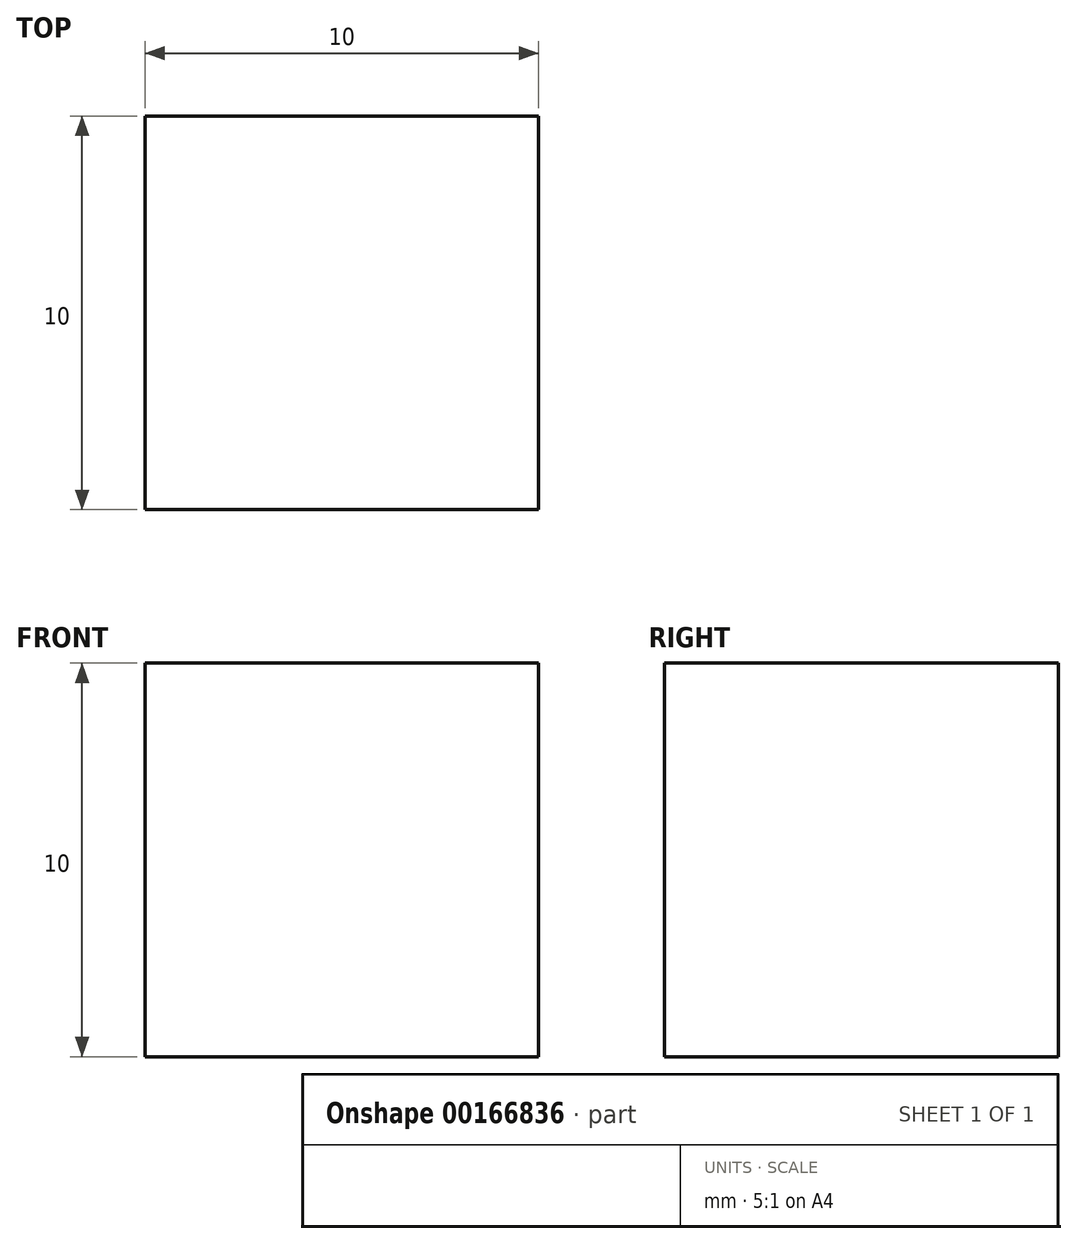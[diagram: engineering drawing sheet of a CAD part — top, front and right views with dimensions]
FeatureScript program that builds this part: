
annotation { "Feature Type Name" : "Feature", "Feature Type Description" : "" }
export const myFeature = defineFeature(function(context is Context, id is Id, definition is map)
    precondition{}
    {
        {
            var Q0;
            Q0=qCreatedBy(makeId("Front.planeOp"),FACE);
            var sketch = newSketch(context, id + "F0", { "sketchPlane" : qUnion([Q0])});
            skLineSegment(sketch, "E0.bottom", {"start": v(5, 5) * mm, "end": v(-5, 5) * mm});
            skLineSegment(sketch, "E0.top", {"start": v(5, -5) * mm, "end": v(-5, -5) * mm});
            skLineSegment(sketch, "E0.left", {"start": v(5, 5) * mm, "end": v(5, -5) * mm});
            skLineSegment(sketch, "E0.right", {"start": v(-5, 5) * mm, "end": v(-5, -5) * mm});
            skPoint(sketch, "E0.middle", {"position": v(0, 0) * mm});
            skSolve(sketch);
        }
        {
            var Q0;
            Q0=makeQuery(id+"F0.imprint","IMPRINT",FACE,{"disambiguationData":[TD([[makeQuery(id+"F0.imprint","IMPRINT",EDGE,{"derivedFrom":sQuery(id+"F0.wireOp",EDGE,"E0.bottom")}),1.0]])]});
            extrude(context, id + "F1", {"entities" : qUnion([Q0]), "depth" : 5 * mm, "hasSecondDirection" : true, "secondDirectionOppositeDirection" : true, "secondDirectionDepth" : 5 * mm});
        }
    });
